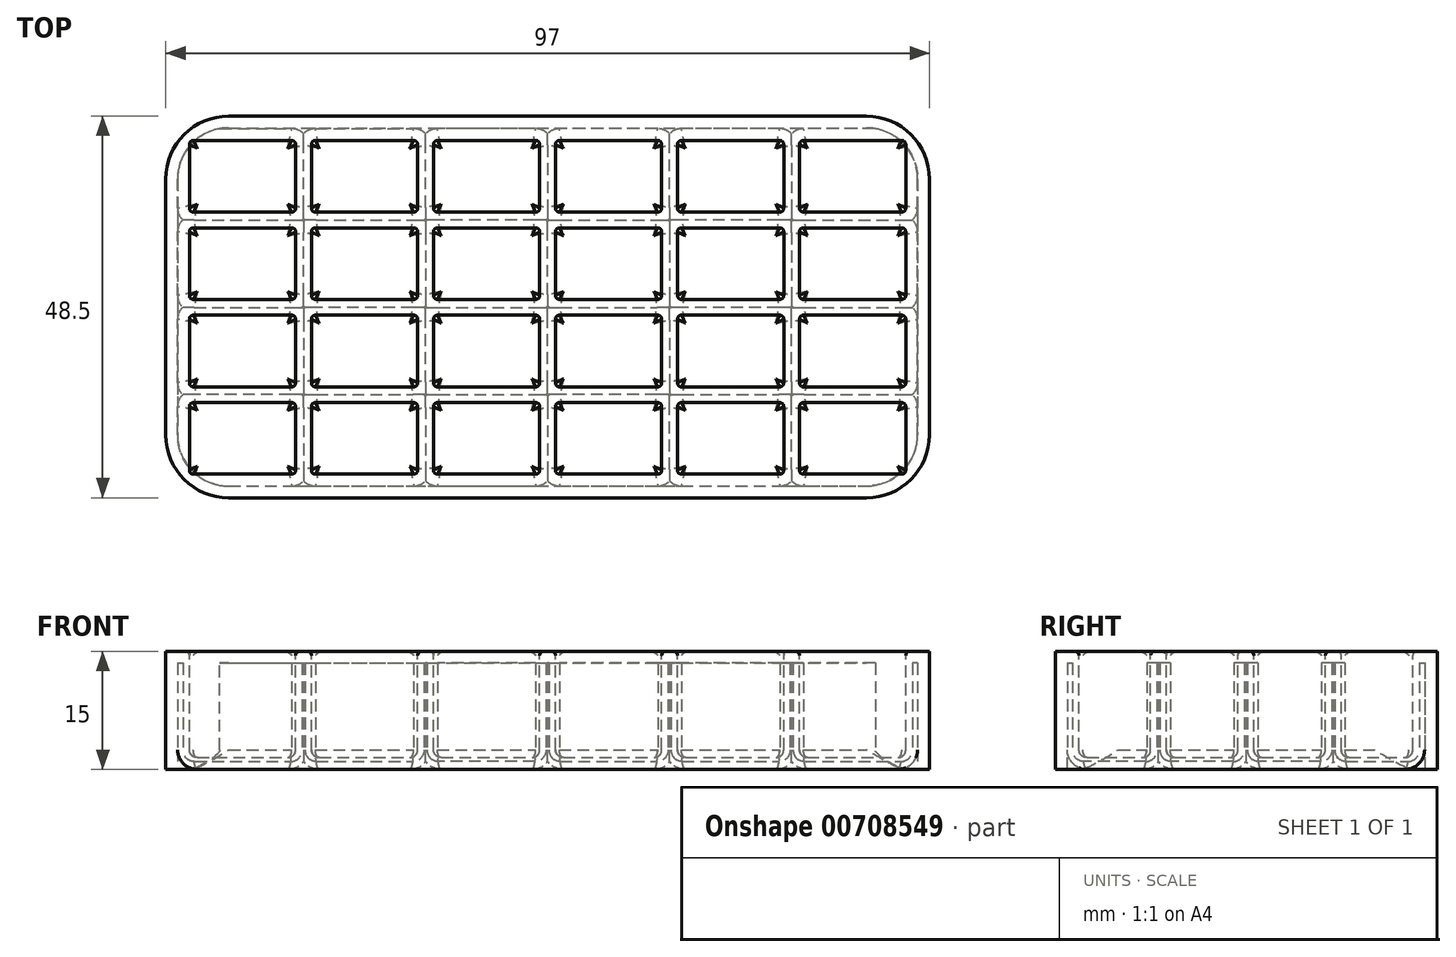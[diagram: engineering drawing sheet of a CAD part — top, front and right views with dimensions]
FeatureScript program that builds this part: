
annotation { "Feature Type Name" : "Feature", "Feature Type Description" : "" }
export const myFeature = defineFeature(function(context is Context, id is Id, definition is map)
    precondition{}
    {
        {
            var Q0;
            Q0=qCreatedBy(makeId("Top.planeOp"),FACE);
            var sketch = newSketch(context, id + "F0", { "sketchPlane" : qUnion([Q0])});
            skLineSegment(sketch, "E0.bottom", {"start": v(-13.12, 43.46) * mm, "end": v(83.88, 43.46) * mm});
            skLineSegment(sketch, "E0.top", {"start": v(-13.12, -5.04) * mm, "end": v(83.88, -5.04) * mm});
            skLineSegment(sketch, "E0.left", {"start": v(-13.12, 43.46) * mm, "end": v(-13.12, -5.04) * mm});
            skLineSegment(sketch, "E0.right", {"start": v(83.88, 43.46) * mm, "end": v(83.88, -5.04) * mm});
            skSolve(sketch);
        }
        {
            var Q0;
            Q0=makeQuery(id+"F0.imprint","IMPRINT",FACE,{"disambiguationData":[TD([[makeQuery(id+"F0.imprint","IMPRINT",EDGE,{"derivedFrom":sQuery(id+"F0.wireOp",EDGE,"E0.bottom")}),-1.0]])]});
            extrude(context, id + "F1", {"entities" : qUnion([Q0]), "depth" : 15 * mm, "offsetDistance" : 25.4 * mm});
        }
        {
            var Q0;
            Q0=makeQuery(id+"F1.opExtrude","CAP_FACE",FACE,{"disambiguationData":[OSD([sQuery(id+"F0.wireOp",EDGE,"E0.bottom"),sQuery(id+"F0.wireOp",EDGE,"E0.top"),sQuery(id+"F0.wireOp",EDGE,"E0.left"),sQuery(id+"F0.wireOp",EDGE,"E0.right")])],"isStart":false});
            var sketch = newSketch(context, id + "F2", { "sketchPlane" : qUnion([Q0])});
            skLineSegment(sketch, "E1.bottom", {"start": v(-10.12, -2.04) * mm, "end": v(3.38, -2.04) * mm});
            skLineSegment(sketch, "E1.top", {"start": v(-10.12, 7.06) * mm, "end": v(3.38, 7.06) * mm});
            skLineSegment(sketch, "E1.left", {"start": v(-10.12, -2.04) * mm, "end": v(-10.12, 7.06) * mm});
            skLineSegment(sketch, "E1.right", {"start": v(3.38, -2.04) * mm, "end": v(3.38, 7.06) * mm});
            skLineSegment(sketch, "E2.1.0.0", {"start": v(18.88, -2.04) * mm, "end": v(18.88, 7.06) * mm});
            skLineSegment(sketch, "E2.1.0.1", {"start": v(5.38, 7.06) * mm, "end": v(18.88, 7.06) * mm});
            skLineSegment(sketch, "E2.1.0.2", {"start": v(5.38, -2.04) * mm, "end": v(5.38, 7.06) * mm});
            skLineSegment(sketch, "E2.1.0.3", {"start": v(5.38, -2.04) * mm, "end": v(18.88, -2.04) * mm});
            skLineSegment(sketch, "E2.2.0.0", {"start": v(34.38, -2.04) * mm, "end": v(34.38, 7.06) * mm});
            skLineSegment(sketch, "E2.2.0.1", {"start": v(20.88, 7.06) * mm, "end": v(34.38, 7.06) * mm});
            skLineSegment(sketch, "E2.2.0.2", {"start": v(20.88, -2.04) * mm, "end": v(20.88, 7.06) * mm});
            skLineSegment(sketch, "E2.2.0.3", {"start": v(20.88, -2.04) * mm, "end": v(34.38, -2.04) * mm});
            skLineSegment(sketch, "E2.3.0.0", {"start": v(49.88, -2.04) * mm, "end": v(49.88, 7.06) * mm});
            skLineSegment(sketch, "E2.3.0.1", {"start": v(36.38, 7.06) * mm, "end": v(49.88, 7.06) * mm});
            skLineSegment(sketch, "E2.3.0.2", {"start": v(36.38, -2.04) * mm, "end": v(36.38, 7.06) * mm});
            skLineSegment(sketch, "E2.3.0.3", {"start": v(36.38, -2.04) * mm, "end": v(49.88, -2.04) * mm});
            skLineSegment(sketch, "E2.4.0.0", {"start": v(65.38, -2.04) * mm, "end": v(65.38, 7.06) * mm});
            skLineSegment(sketch, "E2.4.0.1", {"start": v(51.88, 7.06) * mm, "end": v(65.38, 7.06) * mm});
            skLineSegment(sketch, "E2.4.0.2", {"start": v(51.88, -2.04) * mm, "end": v(51.88, 7.06) * mm});
            skLineSegment(sketch, "E2.4.0.3", {"start": v(51.88, -2.04) * mm, "end": v(65.38, -2.04) * mm});
            skLineSegment(sketch, "E2.5.0.0", {"start": v(80.88, -2.04) * mm, "end": v(80.88, 7.06) * mm});
            skLineSegment(sketch, "E2.5.0.1", {"start": v(67.38, 7.06) * mm, "end": v(80.88, 7.06) * mm});
            skLineSegment(sketch, "E2.5.0.2", {"start": v(67.38, -2.04) * mm, "end": v(67.38, 7.06) * mm});
            skLineSegment(sketch, "E2.5.0.3", {"start": v(67.38, -2.04) * mm, "end": v(80.88, -2.04) * mm});
            skLineSegment(sketch, "E2.direction1", {"start": v(3.38, -2.04) * mm, "end": v(18.88, -2.04) * mm, "construction": true});
            skLineSegment(sketch, "E3.1.0.0", {"start": v(20.88, 9.06) * mm, "end": v(34.38, 9.06) * mm});
            skLineSegment(sketch, "E3.1.0.1", {"start": v(20.88, 9.06) * mm, "end": v(20.88, 18.16) * mm});
            skLineSegment(sketch, "E3.1.0.2", {"start": v(20.88, 18.16) * mm, "end": v(34.38, 18.16) * mm});
            skLineSegment(sketch, "E3.1.0.3", {"start": v(34.38, 9.06) * mm, "end": v(34.38, 18.16) * mm});
            skLineSegment(sketch, "E3.1.0.4", {"start": v(3.38, 9.06) * mm, "end": v(3.38, 18.16) * mm});
            skLineSegment(sketch, "E3.1.0.5", {"start": v(-10.12, 9.06) * mm, "end": v(-10.12, 18.16) * mm});
            skLineSegment(sketch, "E3.1.0.6", {"start": v(-10.12, 18.16) * mm, "end": v(3.38, 18.16) * mm});
            skLineSegment(sketch, "E3.1.0.7", {"start": v(36.38, 9.06) * mm, "end": v(36.38, 18.16) * mm});
            skLineSegment(sketch, "E3.1.0.8", {"start": v(-10.12, 9.06) * mm, "end": v(3.38, 9.06) * mm});
            skLineSegment(sketch, "E3.1.0.9", {"start": v(36.38, 18.16) * mm, "end": v(49.88, 18.16) * mm});
            skLineSegment(sketch, "E3.1.0.10", {"start": v(51.88, 9.06) * mm, "end": v(51.88, 18.16) * mm});
            skLineSegment(sketch, "E3.1.0.11", {"start": v(65.38, 9.06) * mm, "end": v(65.38, 18.16) * mm});
            skLineSegment(sketch, "E3.1.0.12", {"start": v(67.38, 18.16) * mm, "end": v(80.88, 18.16) * mm});
            skLineSegment(sketch, "E3.1.0.13", {"start": v(51.88, 9.06) * mm, "end": v(65.38, 9.06) * mm});
            skLineSegment(sketch, "E3.1.0.14", {"start": v(67.38, 9.06) * mm, "end": v(67.38, 18.16) * mm});
            skLineSegment(sketch, "E3.1.0.15", {"start": v(18.88, 9.06) * mm, "end": v(18.88, 18.16) * mm});
            skLineSegment(sketch, "E3.1.0.16", {"start": v(5.38, 18.16) * mm, "end": v(18.88, 18.16) * mm});
            skLineSegment(sketch, "E3.1.0.17", {"start": v(67.38, 9.06) * mm, "end": v(80.88, 9.06) * mm});
            skLineSegment(sketch, "E3.1.0.18", {"start": v(36.38, 9.06) * mm, "end": v(49.88, 9.06) * mm});
            skLineSegment(sketch, "E3.1.0.19", {"start": v(49.88, 9.06) * mm, "end": v(49.88, 18.16) * mm});
            skLineSegment(sketch, "E3.1.0.20", {"start": v(80.88, 9.06) * mm, "end": v(80.88, 18.16) * mm});
            skLineSegment(sketch, "E3.1.0.21", {"start": v(5.38, 9.06) * mm, "end": v(5.38, 18.16) * mm});
            skLineSegment(sketch, "E3.1.0.22", {"start": v(51.88, 18.16) * mm, "end": v(65.38, 18.16) * mm});
            skLineSegment(sketch, "E3.1.0.23", {"start": v(3.38, 9.06) * mm, "end": v(18.88, 9.06) * mm, "construction": true});
            skLineSegment(sketch, "E3.1.0.24", {"start": v(5.38, 9.06) * mm, "end": v(18.88, 9.06) * mm});
            skLineSegment(sketch, "E3.2.0.0", {"start": v(20.88, 20.16) * mm, "end": v(34.38, 20.16) * mm});
            skLineSegment(sketch, "E3.2.0.1", {"start": v(20.88, 20.16) * mm, "end": v(20.88, 29.26) * mm});
            skLineSegment(sketch, "E3.2.0.2", {"start": v(20.88, 29.26) * mm, "end": v(34.38, 29.26) * mm});
            skLineSegment(sketch, "E3.2.0.3", {"start": v(34.38, 20.16) * mm, "end": v(34.38, 29.26) * mm});
            skLineSegment(sketch, "E3.2.0.4", {"start": v(3.38, 20.16) * mm, "end": v(3.38, 29.26) * mm});
            skLineSegment(sketch, "E3.2.0.5", {"start": v(-10.12, 20.16) * mm, "end": v(-10.12, 29.26) * mm});
            skLineSegment(sketch, "E3.2.0.6", {"start": v(-10.12, 29.26) * mm, "end": v(3.38, 29.26) * mm});
            skLineSegment(sketch, "E3.2.0.7", {"start": v(36.38, 20.16) * mm, "end": v(36.38, 29.26) * mm});
            skLineSegment(sketch, "E3.2.0.8", {"start": v(-10.12, 20.16) * mm, "end": v(3.38, 20.16) * mm});
            skLineSegment(sketch, "E3.2.0.9", {"start": v(36.38, 29.26) * mm, "end": v(49.88, 29.26) * mm});
            skLineSegment(sketch, "E3.2.0.10", {"start": v(51.88, 20.16) * mm, "end": v(51.88, 29.26) * mm});
            skLineSegment(sketch, "E3.2.0.11", {"start": v(65.38, 20.16) * mm, "end": v(65.38, 29.26) * mm});
            skLineSegment(sketch, "E3.2.0.12", {"start": v(67.38, 29.26) * mm, "end": v(80.88, 29.26) * mm});
            skLineSegment(sketch, "E3.2.0.13", {"start": v(51.88, 20.16) * mm, "end": v(65.38, 20.16) * mm});
            skLineSegment(sketch, "E3.2.0.14", {"start": v(67.38, 20.16) * mm, "end": v(67.38, 29.26) * mm});
            skLineSegment(sketch, "E3.2.0.15", {"start": v(18.88, 20.16) * mm, "end": v(18.88, 29.26) * mm});
            skLineSegment(sketch, "E3.2.0.16", {"start": v(5.38, 29.26) * mm, "end": v(18.88, 29.26) * mm});
            skLineSegment(sketch, "E3.2.0.17", {"start": v(67.38, 20.16) * mm, "end": v(80.88, 20.16) * mm});
            skLineSegment(sketch, "E3.2.0.18", {"start": v(36.38, 20.16) * mm, "end": v(49.88, 20.16) * mm});
            skLineSegment(sketch, "E3.2.0.19", {"start": v(49.88, 20.16) * mm, "end": v(49.88, 29.26) * mm});
            skLineSegment(sketch, "E3.2.0.20", {"start": v(80.88, 20.16) * mm, "end": v(80.88, 29.26) * mm});
            skLineSegment(sketch, "E3.2.0.21", {"start": v(5.38, 20.16) * mm, "end": v(5.38, 29.26) * mm});
            skLineSegment(sketch, "E3.2.0.22", {"start": v(51.88, 29.26) * mm, "end": v(65.38, 29.26) * mm});
            skLineSegment(sketch, "E3.2.0.23", {"start": v(3.38, 20.16) * mm, "end": v(18.88, 20.16) * mm, "construction": true});
            skLineSegment(sketch, "E3.2.0.24", {"start": v(5.38, 20.16) * mm, "end": v(18.88, 20.16) * mm});
            skLineSegment(sketch, "E3.direction1", {"start": v(-10.12, -2.04) * mm, "end": v(-10.12, 9.06) * mm, "construction": true});
            skLineSegment(sketch, "E4.0.3.0", {"start": v(20.88, 31.26) * mm, "end": v(34.38, 31.26) * mm});
            skLineSegment(sketch, "E4.3.3.0", {"start": v(20.88, 31.26) * mm, "end": v(20.88, 40.36) * mm});
            skLineSegment(sketch, "E4.6.3.0", {"start": v(20.88, 40.36) * mm, "end": v(34.38, 40.36) * mm});
            skLineSegment(sketch, "E4.9.3.0", {"start": v(34.38, 31.26) * mm, "end": v(34.38, 40.36) * mm});
            skLineSegment(sketch, "E4.12.3.0", {"start": v(3.38, 31.26) * mm, "end": v(3.38, 40.36) * mm});
            skLineSegment(sketch, "E4.15.3.0", {"start": v(-10.12, 31.26) * mm, "end": v(-10.12, 40.36) * mm});
            skLineSegment(sketch, "E4.18.3.0", {"start": v(-10.12, 40.36) * mm, "end": v(3.38, 40.36) * mm});
            skLineSegment(sketch, "E4.21.3.0", {"start": v(36.38, 31.26) * mm, "end": v(36.38, 40.36) * mm});
            skLineSegment(sketch, "E4.24.3.0", {"start": v(-10.12, 31.26) * mm, "end": v(3.38, 31.26) * mm});
            skLineSegment(sketch, "E4.27.3.0", {"start": v(36.38, 40.36) * mm, "end": v(49.88, 40.36) * mm});
            skLineSegment(sketch, "E4.30.3.0", {"start": v(51.88, 31.26) * mm, "end": v(51.88, 40.36) * mm});
            skLineSegment(sketch, "E4.33.3.0", {"start": v(65.38, 31.26) * mm, "end": v(65.38, 40.36) * mm});
            skLineSegment(sketch, "E4.36.3.0", {"start": v(67.38, 40.36) * mm, "end": v(80.88, 40.36) * mm});
            skLineSegment(sketch, "E4.39.3.0", {"start": v(51.88, 31.26) * mm, "end": v(65.38, 31.26) * mm});
            skLineSegment(sketch, "E4.42.3.0", {"start": v(67.38, 31.26) * mm, "end": v(67.38, 40.36) * mm});
            skLineSegment(sketch, "E4.45.3.0", {"start": v(18.88, 31.26) * mm, "end": v(18.88, 40.36) * mm});
            skLineSegment(sketch, "E4.48.3.0", {"start": v(5.38, 40.36) * mm, "end": v(18.88, 40.36) * mm});
            skLineSegment(sketch, "E4.51.3.0", {"start": v(67.38, 31.26) * mm, "end": v(80.88, 31.26) * mm});
            skLineSegment(sketch, "E4.54.3.0", {"start": v(36.38, 31.26) * mm, "end": v(49.88, 31.26) * mm});
            skLineSegment(sketch, "E4.57.3.0", {"start": v(49.88, 31.26) * mm, "end": v(49.88, 40.36) * mm});
            skLineSegment(sketch, "E4.60.3.0", {"start": v(80.88, 31.26) * mm, "end": v(80.88, 40.36) * mm});
            skLineSegment(sketch, "E4.63.3.0", {"start": v(5.38, 31.26) * mm, "end": v(5.38, 40.36) * mm});
            skLineSegment(sketch, "E4.66.3.0", {"start": v(51.88, 40.36) * mm, "end": v(65.38, 40.36) * mm});
            skLineSegment(sketch, "E4.69.3.0", {"start": v(3.38, 31.26) * mm, "end": v(18.88, 31.26) * mm, "construction": true});
            skLineSegment(sketch, "E4.72.3.0", {"start": v(5.38, 31.26) * mm, "end": v(18.88, 31.26) * mm});
            skSolve(sketch);
        }
        {
            var Q0;
            Q0=makeQuery(id+"F2.imprint","IMPRINT",FACE,{"disambiguationData":[TD([[makeQuery(id+"F2.imprint","IMPRINT",EDGE,{"derivedFrom":sQuery(id+"F2.wireOp",EDGE,"E1.bottom")}),1.0]])]});
            var Q1;
            Q1=makeQuery(id+"F2.imprint","IMPRINT",FACE,{"disambiguationData":[TD([[makeQuery(id+"F2.imprint","IMPRINT",EDGE,{"derivedFrom":sQuery(id+"F2.wireOp",EDGE,"E2.1.0.0")}),1.0]])]});
            var Q2;
            Q2=makeQuery(id+"F2.imprint","IMPRINT",FACE,{"disambiguationData":[TD([[makeQuery(id+"F2.imprint","IMPRINT",EDGE,{"derivedFrom":sQuery(id+"F2.wireOp",EDGE,"E2.2.0.0")}),1.0]])]});
            var Q3;
            Q3=makeQuery(id+"F2.imprint","IMPRINT",FACE,{"disambiguationData":[TD([[makeQuery(id+"F2.imprint","IMPRINT",EDGE,{"derivedFrom":sQuery(id+"F2.wireOp",EDGE,"E2.3.0.0")}),1.0]])]});
            var Q4;
            Q4=makeQuery(id+"F2.imprint","IMPRINT",FACE,{"disambiguationData":[TD([[makeQuery(id+"F2.imprint","IMPRINT",EDGE,{"derivedFrom":sQuery(id+"F2.wireOp",EDGE,"E2.4.0.0")}),1.0]])]});
            var Q5;
            Q5=makeQuery(id+"F2.imprint","IMPRINT",FACE,{"disambiguationData":[TD([[makeQuery(id+"F2.imprint","IMPRINT",EDGE,{"derivedFrom":sQuery(id+"F2.wireOp",EDGE,"E2.5.0.0")}),1.0]])]});
            var Q6;
            Q6=makeQuery(id+"F2.imprint","IMPRINT",FACE,{"disambiguationData":[TD([[makeQuery(id+"F2.imprint","IMPRINT",EDGE,{"derivedFrom":sQuery(id+"F2.wireOp",EDGE,"E3.1.0.4")}),1.0]])]});
            var Q7;
            Q7=makeQuery(id+"F2.imprint","IMPRINT",FACE,{"disambiguationData":[TD([[makeQuery(id+"F2.imprint","IMPRINT",EDGE,{"derivedFrom":sQuery(id+"F2.wireOp",EDGE,"E3.1.0.15")}),1.0]])]});
            var Q8;
            Q8=makeQuery(id+"F2.imprint","IMPRINT",FACE,{"disambiguationData":[TD([[makeQuery(id+"F2.imprint","IMPRINT",EDGE,{"derivedFrom":sQuery(id+"F2.wireOp",EDGE,"E3.2.0.7")}),-1.0]])]});
            var Q9;
            Q9=makeQuery(id+"F2.imprint","IMPRINT",FACE,{"disambiguationData":[TD([[makeQuery(id+"F2.imprint","IMPRINT",EDGE,{"derivedFrom":sQuery(id+"F2.wireOp",EDGE,"E3.1.0.0")}),1.0]])]});
            var Q10;
            Q10=makeQuery(id+"F2.imprint","IMPRINT",FACE,{"disambiguationData":[TD([[makeQuery(id+"F2.imprint","IMPRINT",EDGE,{"derivedFrom":sQuery(id+"F2.wireOp",EDGE,"E3.1.0.7")}),-1.0]])]});
            var Q11;
            Q11=makeQuery(id+"F2.imprint","IMPRINT",FACE,{"disambiguationData":[TD([[makeQuery(id+"F2.imprint","IMPRINT",EDGE,{"derivedFrom":sQuery(id+"F2.wireOp",EDGE,"E3.1.0.10")}),-1.0]])]});
            var Q12;
            Q12=makeQuery(id+"F2.imprint","IMPRINT",FACE,{"disambiguationData":[TD([[makeQuery(id+"F2.imprint","IMPRINT",EDGE,{"derivedFrom":sQuery(id+"F2.wireOp",EDGE,"E3.1.0.12")}),-1.0]])]});
            var Q13;
            Q13=makeQuery(id+"F2.imprint","IMPRINT",FACE,{"disambiguationData":[TD([[makeQuery(id+"F2.imprint","IMPRINT",EDGE,{"derivedFrom":sQuery(id+"F2.wireOp",EDGE,"E3.2.0.12")}),-1.0]])]});
            var Q14;
            Q14=makeQuery(id+"F2.imprint","IMPRINT",FACE,{"disambiguationData":[TD([[makeQuery(id+"F2.imprint","IMPRINT",EDGE,{"derivedFrom":sQuery(id+"F2.wireOp",EDGE,"E3.2.0.10")}),-1.0]])]});
            var Q15;
            Q15=makeQuery(id+"F2.imprint","IMPRINT",FACE,{"disambiguationData":[TD([[makeQuery(id+"F2.imprint","IMPRINT",EDGE,{"derivedFrom":sQuery(id+"F2.wireOp",EDGE,"E3.2.0.0")}),1.0]])]});
            var Q16;
            Q16=makeQuery(id+"F2.imprint","IMPRINT",FACE,{"disambiguationData":[TD([[makeQuery(id+"F2.imprint","IMPRINT",EDGE,{"derivedFrom":sQuery(id+"F2.wireOp",EDGE,"E3.2.0.15")}),1.0]])]});
            var Q17;
            Q17=makeQuery(id+"F2.imprint","IMPRINT",FACE,{"disambiguationData":[TD([[makeQuery(id+"F2.imprint","IMPRINT",EDGE,{"derivedFrom":sQuery(id+"F2.wireOp",EDGE,"E3.2.0.4")}),1.0]])]});
            var Q18;
            Q18=makeQuery(id+"F2.imprint","IMPRINT",FACE,{"disambiguationData":[TD([[makeQuery(id+"F2.imprint","IMPRINT",EDGE,{"derivedFrom":sQuery(id+"F2.wireOp",EDGE,"2d819ab5-a139-4a24-9444-a94bec9d9159.0.2.2")}),1.0]])]});
            var Q19;
            Q19=makeQuery(id+"F2.imprint","IMPRINT",FACE,{"disambiguationData":[TD([[makeQuery(id+"F2.imprint","IMPRINT",EDGE,{"derivedFrom":sQuery(id+"F2.wireOp",EDGE,"2d819ab5-a139-4a24-9444-a94bec9d9159.0.2.0")}),1.0]])]});
            var Q20;
            Q20=makeQuery(id+"F2.imprint","IMPRINT",FACE,{"disambiguationData":[TD([[makeQuery(id+"F2.imprint","IMPRINT",EDGE,{"derivedFrom":sQuery(id+"F2.wireOp",EDGE,"2d819ab5-a139-4a24-9444-a94bec9d9159.0.1.0")}),1.0]])]});
            var Q21;
            Q21=makeQuery(id+"F2.imprint","IMPRINT",FACE,{"disambiguationData":[TD([[makeQuery(id+"F2.imprint","IMPRINT",EDGE,{"derivedFrom":sQuery(id+"F2.wireOp",EDGE,"c4168fa5-6cb4-4a63-8e2b-b4d674aba8b3.0.7.0")}),1.0]])]});
            var Q22;
            Q22=makeQuery(id+"F2.imprint","IMPRINT",FACE,{"disambiguationData":[TD([[makeQuery(id+"F2.imprint","IMPRINT",EDGE,{"derivedFrom":sQuery(id+"F2.wireOp",EDGE,"c4168fa5-6cb4-4a63-8e2b-b4d674aba8b3.0.6.0")}),1.0]])]});
            var Q23;
            Q23=makeQuery(id+"F2.imprint","IMPRINT",FACE,{"disambiguationData":[TD([[makeQuery(id+"F2.imprint","IMPRINT",EDGE,{"derivedFrom":sQuery(id+"F2.wireOp",EDGE,"2d819ab5-a139-4a24-9444-a94bec9d9159.0.1.2")}),1.0]])]});
            var Q24;
            Q24=makeQuery(id+"F2.imprint","IMPRINT",FACE,{"disambiguationData":[TD([[makeQuery(id+"F2.imprint","IMPRINT",EDGE,{"derivedFrom":sQuery(id+"F2.wireOp",EDGE,"E4.36.3.0")}),-1.0]])]});
            var Q25;
            Q25=makeQuery(id+"F2.imprint","IMPRINT",FACE,{"disambiguationData":[TD([[makeQuery(id+"F2.imprint","IMPRINT",EDGE,{"derivedFrom":sQuery(id+"F2.wireOp",EDGE,"E4.30.3.0")}),-1.0]])]});
            var Q26;
            Q26=makeQuery(id+"F2.imprint","IMPRINT",FACE,{"disambiguationData":[TD([[makeQuery(id+"F2.imprint","IMPRINT",EDGE,{"derivedFrom":sQuery(id+"F2.wireOp",EDGE,"E4.21.3.0")}),-1.0]])]});
            var Q27;
            Q27=makeQuery(id+"F2.imprint","IMPRINT",FACE,{"disambiguationData":[TD([[makeQuery(id+"F2.imprint","IMPRINT",EDGE,{"derivedFrom":sQuery(id+"F2.wireOp",EDGE,"E4.0.3.0")}),1.0]])]});
            var Q28;
            Q28=makeQuery(id+"F2.imprint","IMPRINT",FACE,{"disambiguationData":[TD([[makeQuery(id+"F2.imprint","IMPRINT",EDGE,{"derivedFrom":sQuery(id+"F2.wireOp",EDGE,"E4.45.3.0")}),1.0]])]});
            var Q29;
            Q29=makeQuery(id+"F2.imprint","IMPRINT",FACE,{"disambiguationData":[TD([[makeQuery(id+"F2.imprint","IMPRINT",EDGE,{"derivedFrom":sQuery(id+"F2.wireOp",EDGE,"E4.12.3.0")}),1.0]])]});
            extrude(context, id + "F3", {"entities" : qUnion([Q0, Q1, Q2, Q3, Q4, Q5, Q6, Q7, Q8, Q9, Q10, Q11, Q12, Q13, Q14, Q15, Q16, Q17, Q18, Q19, Q20, Q21, Q22, Q23, Q24, Q25, Q26, Q27, Q28, Q29]), "operationType" : NewBodyOperationType.REMOVE, "oppositeDirection" : true, "depth" : 13.5 * mm, "offsetDistance" : 25 * mm});
        }
        {
            var Q0;
            Q0=makeQuery(id+"F1.opExtrude","SWEPT_EDGE",EDGE,{"disambiguationData":[OSD([sQuery(id+"F0.wireOp",EDGE,"E0.top"),sQuery(id+"F0.wireOp",EDGE,"E0.left")])]});
            var Q1;
            Q1=makeQuery(id+"F1.opExtrude","SWEPT_EDGE",EDGE,{"disambiguationData":[OSD([sQuery(id+"F0.wireOp",EDGE,"E0.top"),sQuery(id+"F0.wireOp",EDGE,"E0.right")])]});
            var Q2;
            Q2=makeQuery(id+"F1.opExtrude","SWEPT_EDGE",EDGE,{"disambiguationData":[OSD([sQuery(id+"F0.wireOp",EDGE,"E0.bottom"),sQuery(id+"F0.wireOp",EDGE,"E0.right")])]});
            var Q3;
            Q3=makeQuery(id+"F1.opExtrude","SWEPT_EDGE",EDGE,{"disambiguationData":[OSD([sQuery(id+"F0.wireOp",EDGE,"E0.bottom"),sQuery(id+"F0.wireOp",EDGE,"E0.left")])]});
            fillet(context, id + "F4", {"entities" : qUnion([Q0, Q1, Q2, Q3]), "radius" : 8 * mm, "tangentPropagation" : true, "allowEdgeOverflow" : false});
        }
        {
            var Q0;
            Q0=makeQuery(id+"F3.boolean.opBoolean","COPY",EDGE,{"derivedFrom":makeQuery(id+"F3.opExtrude","CAP_EDGE",EDGE,{"disambiguationData":[OSD([sQuery(id+"F2.wireOp",EDGE,"E3.1.0.22")])],"isStart":false})});
            var Q1;
            Q1=makeQuery(id+"F3.boolean.opBoolean","COPY",EDGE,{"derivedFrom":makeQuery(id+"F3.opExtrude","CAP_EDGE",EDGE,{"disambiguationData":[OSD([sQuery(id+"F2.wireOp",EDGE,"E3.1.0.11")])],"isStart":false})});
            var Q2;
            Q2=makeQuery(id+"F3.boolean.opBoolean","COPY",EDGE,{"derivedFrom":makeQuery(id+"F3.opExtrude","CAP_EDGE",EDGE,{"disambiguationData":[OSD([sQuery(id+"F2.wireOp",EDGE,"E3.1.0.13")])],"isStart":false})});
            var Q3;
            Q3=makeQuery(id+"F3.boolean.opBoolean","COPY",EDGE,{"derivedFrom":makeQuery(id+"F3.opExtrude","CAP_EDGE",EDGE,{"disambiguationData":[OSD([sQuery(id+"F2.wireOp",EDGE,"E3.1.0.10")])],"isStart":false})});
            var Q4;
            Q4=makeQuery(id+"F3.boolean.opBoolean","COPY",EDGE,{"derivedFrom":makeQuery(id+"F3.opExtrude","CAP_EDGE",EDGE,{"disambiguationData":[OSD([sQuery(id+"F2.wireOp",EDGE,"E3.2.0.22")])],"isStart":false})});
            var Q5;
            Q5=makeQuery(id+"F3.boolean.opBoolean","COPY",EDGE,{"derivedFrom":makeQuery(id+"F3.opExtrude","CAP_EDGE",EDGE,{"disambiguationData":[OSD([sQuery(id+"F2.wireOp",EDGE,"E3.2.0.11")])],"isStart":false})});
            var Q6;
            Q6=makeQuery(id+"F3.boolean.opBoolean","COPY",FACE,{"derivedFrom":makeQuery(id+"F3.opExtrude","CAP_FACE",FACE,{"disambiguationData":[OSD([sQuery(id+"F2.wireOp",EDGE,"E3.2.0.10"),sQuery(id+"F2.wireOp",EDGE,"E3.2.0.11"),sQuery(id+"F2.wireOp",EDGE,"E3.2.0.13"),sQuery(id+"F2.wireOp",EDGE,"E3.2.0.22")])],"isStart":false})});
            var Q7;
            Q7=makeQuery(id+"F3.boolean.opBoolean","COPY",FACE,{"derivedFrom":makeQuery(id+"F3.opExtrude","CAP_FACE",FACE,{"disambiguationData":[OSD([sQuery(id+"F2.wireOp",EDGE,"E2.4.0.0"),sQuery(id+"F2.wireOp",EDGE,"E2.4.0.1"),sQuery(id+"F2.wireOp",EDGE,"E2.4.0.2"),sQuery(id+"F2.wireOp",EDGE,"E2.4.0.3")])],"isStart":false})});
            var Q8;
            Q8=makeQuery(id+"F3.boolean.opBoolean","COPY",FACE,{"derivedFrom":makeQuery(id+"F3.opExtrude","CAP_FACE",FACE,{"disambiguationData":[OSD([sQuery(id+"F2.wireOp",EDGE,"E2.3.0.0"),sQuery(id+"F2.wireOp",EDGE,"E2.3.0.1"),sQuery(id+"F2.wireOp",EDGE,"E2.3.0.2"),sQuery(id+"F2.wireOp",EDGE,"E2.3.0.3")])],"isStart":false})});
            var Q9;
            Q9=makeQuery(id+"F3.boolean.opBoolean","COPY",FACE,{"derivedFrom":makeQuery(id+"F3.opExtrude","CAP_FACE",FACE,{"disambiguationData":[OSD([sQuery(id+"F2.wireOp",EDGE,"E3.1.0.7"),sQuery(id+"F2.wireOp",EDGE,"E3.1.0.9"),sQuery(id+"F2.wireOp",EDGE,"E3.1.0.18"),sQuery(id+"F2.wireOp",EDGE,"E3.1.0.19")])],"isStart":false})});
            var Q10;
            Q10=makeQuery(id+"F3.boolean.opBoolean","COPY",FACE,{"derivedFrom":makeQuery(id+"F3.opExtrude","CAP_FACE",FACE,{"disambiguationData":[OSD([sQuery(id+"F2.wireOp",EDGE,"E3.2.0.7"),sQuery(id+"F2.wireOp",EDGE,"E3.2.0.9"),sQuery(id+"F2.wireOp",EDGE,"E3.2.0.18"),sQuery(id+"F2.wireOp",EDGE,"E3.2.0.19")])],"isStart":false})});
            var Q11;
            Q11=makeQuery(id+"F3.boolean.opBoolean","COPY",FACE,{"derivedFrom":makeQuery(id+"F3.opExtrude","CAP_FACE",FACE,{"disambiguationData":[OSD([sQuery(id+"F2.wireOp",EDGE,"E3.2.0.0"),sQuery(id+"F2.wireOp",EDGE,"E3.2.0.1"),sQuery(id+"F2.wireOp",EDGE,"E3.2.0.2"),sQuery(id+"F2.wireOp",EDGE,"E3.2.0.3")])],"isStart":false})});
            var Q12;
            Q12=makeQuery(id+"F3.boolean.opBoolean","COPY",FACE,{"derivedFrom":makeQuery(id+"F3.opExtrude","CAP_FACE",FACE,{"disambiguationData":[OSD([sQuery(id+"F2.wireOp",EDGE,"E3.1.0.0"),sQuery(id+"F2.wireOp",EDGE,"E3.1.0.1"),sQuery(id+"F2.wireOp",EDGE,"E3.1.0.2"),sQuery(id+"F2.wireOp",EDGE,"E3.1.0.3")])],"isStart":false})});
            var Q13;
            Q13=makeQuery(id+"F3.boolean.opBoolean","COPY",FACE,{"derivedFrom":makeQuery(id+"F3.opExtrude","CAP_FACE",FACE,{"disambiguationData":[OSD([sQuery(id+"F2.wireOp",EDGE,"E2.2.0.0"),sQuery(id+"F2.wireOp",EDGE,"E2.2.0.1"),sQuery(id+"F2.wireOp",EDGE,"E2.2.0.2"),sQuery(id+"F2.wireOp",EDGE,"E2.2.0.3")])],"isStart":false})});
            var Q14;
            Q14=makeQuery(id+"F3.boolean.opBoolean","COPY",FACE,{"derivedFrom":makeQuery(id+"F3.opExtrude","CAP_FACE",FACE,{"disambiguationData":[OSD([sQuery(id+"F2.wireOp",EDGE,"E2.1.0.0"),sQuery(id+"F2.wireOp",EDGE,"E2.1.0.1"),sQuery(id+"F2.wireOp",EDGE,"E2.1.0.2"),sQuery(id+"F2.wireOp",EDGE,"E2.1.0.3")])],"isStart":false})});
            var Q15;
            Q15=makeQuery(id+"F3.boolean.opBoolean","COPY",FACE,{"derivedFrom":makeQuery(id+"F3.opExtrude","CAP_FACE",FACE,{"disambiguationData":[OSD([sQuery(id+"F2.wireOp",EDGE,"E3.1.0.4"),sQuery(id+"F2.wireOp",EDGE,"E3.1.0.5"),sQuery(id+"F2.wireOp",EDGE,"E3.1.0.6"),sQuery(id+"F2.wireOp",EDGE,"E3.1.0.8")])],"isStart":false})});
            var Q16;
            Q16=makeQuery(id+"F3.boolean.opBoolean","COPY",FACE,{"derivedFrom":makeQuery(id+"F3.opExtrude","CAP_FACE",FACE,{"disambiguationData":[OSD([sQuery(id+"F2.wireOp",EDGE,"E3.1.0.15"),sQuery(id+"F2.wireOp",EDGE,"E3.1.0.16"),sQuery(id+"F2.wireOp",EDGE,"E3.1.0.21"),sQuery(id+"F2.wireOp",EDGE,"E3.1.0.24")])],"isStart":false})});
            var Q17;
            Q17=makeQuery(id+"F3.boolean.opBoolean","COPY",FACE,{"derivedFrom":makeQuery(id+"F3.opExtrude","CAP_FACE",FACE,{"disambiguationData":[OSD([sQuery(id+"F2.wireOp",EDGE,"E3.2.0.15"),sQuery(id+"F2.wireOp",EDGE,"E3.2.0.16"),sQuery(id+"F2.wireOp",EDGE,"E3.2.0.21"),sQuery(id+"F2.wireOp",EDGE,"E3.2.0.24")])],"isStart":false})});
            var Q18;
            Q18=makeQuery(id+"F3.boolean.opBoolean","COPY",FACE,{"derivedFrom":makeQuery(id+"F3.opExtrude","CAP_FACE",FACE,{"disambiguationData":[OSD([sQuery(id+"F2.wireOp",EDGE,"E3.2.0.4"),sQuery(id+"F2.wireOp",EDGE,"E3.2.0.5"),sQuery(id+"F2.wireOp",EDGE,"E3.2.0.6"),sQuery(id+"F2.wireOp",EDGE,"E3.2.0.8")])],"isStart":false})});
            var Q19;
            Q19=makeQuery(id+"F3.boolean.opBoolean","COPY",FACE,{"derivedFrom":makeQuery(id+"F3.opExtrude","CAP_FACE",FACE,{"disambiguationData":[OSD([sQuery(id+"F2.wireOp",EDGE,"E1.bottom"),sQuery(id+"F2.wireOp",EDGE,"E1.top"),sQuery(id+"F2.wireOp",EDGE,"E1.left"),sQuery(id+"F2.wireOp",EDGE,"E1.right")])],"isStart":false})});
            var Q20;
            Q20=makeQuery(id+"F3.boolean.opBoolean","COPY",EDGE,{"derivedFrom":makeQuery(id+"F3.opExtrude","CAP_EDGE",EDGE,{"disambiguationData":[OSD([sQuery(id+"F2.wireOp",EDGE,"E3.2.0.12")])],"isStart":false})});
            var Q21;
            Q21=makeQuery(id+"F3.boolean.opBoolean","COPY",FACE,{"derivedFrom":makeQuery(id+"F3.opExtrude","CAP_FACE",FACE,{"disambiguationData":[OSD([sQuery(id+"F2.wireOp",EDGE,"2d819ab5-a139-4a24-9444-a94bec9d9159.0.2.2"),sQuery(id+"F2.wireOp",EDGE,"2d819ab5-a139-4a24-9444-a94bec9d9159.0.2.3"),sQuery(id+"F2.wireOp",EDGE,"2d819ab5-a139-4a24-9444-a94bec9d9159.0.2.4"),sQuery(id+"F2.wireOp",EDGE,"2d819ab5-a139-4a24-9444-a94bec9d9159.0.2.5")])],"isStart":false})});
            var Q22;
            Q22=makeQuery(id+"F3.boolean.opBoolean","COPY",FACE,{"derivedFrom":makeQuery(id+"F3.opExtrude","CAP_FACE",FACE,{"disambiguationData":[OSD([sQuery(id+"F2.wireOp",EDGE,"E3.2.0.12"),sQuery(id+"F2.wireOp",EDGE,"E3.2.0.14"),sQuery(id+"F2.wireOp",EDGE,"E3.2.0.17"),sQuery(id+"F2.wireOp",EDGE,"E3.2.0.20")])],"isStart":false})});
            var Q23;
            Q23=makeQuery(id+"F3.boolean.opBoolean","COPY",FACE,{"derivedFrom":makeQuery(id+"F3.opExtrude","CAP_FACE",FACE,{"disambiguationData":[OSD([sQuery(id+"F2.wireOp",EDGE,"2d819ab5-a139-4a24-9444-a94bec9d9159.0.2.0"),sQuery(id+"F2.wireOp",EDGE,"2d819ab5-a139-4a24-9444-a94bec9d9159.0.2.1"),sQuery(id+"F2.wireOp",EDGE,"2d819ab5-a139-4a24-9444-a94bec9d9159.0.2.6"),sQuery(id+"F2.wireOp",EDGE,"2d819ab5-a139-4a24-9444-a94bec9d9159.0.2.7")])],"isStart":false})});
            var Q24;
            Q24=makeQuery(id+"F3.boolean.opBoolean","COPY",FACE,{"derivedFrom":makeQuery(id+"F3.opExtrude","CAP_FACE",FACE,{"disambiguationData":[OSD([sQuery(id+"F2.wireOp",EDGE,"2d819ab5-a139-4a24-9444-a94bec9d9159.0.1.0"),sQuery(id+"F2.wireOp",EDGE,"2d819ab5-a139-4a24-9444-a94bec9d9159.0.1.1"),sQuery(id+"F2.wireOp",EDGE,"2d819ab5-a139-4a24-9444-a94bec9d9159.0.1.6"),sQuery(id+"F2.wireOp",EDGE,"2d819ab5-a139-4a24-9444-a94bec9d9159.0.1.7")])],"isStart":false})});
            var Q25;
            Q25=makeQuery(id+"F3.boolean.opBoolean","COPY",FACE,{"derivedFrom":makeQuery(id+"F3.opExtrude","CAP_FACE",FACE,{"disambiguationData":[OSD([sQuery(id+"F2.wireOp",EDGE,"2d819ab5-a139-4a24-9444-a94bec9d9159.0.1.2"),sQuery(id+"F2.wireOp",EDGE,"2d819ab5-a139-4a24-9444-a94bec9d9159.0.1.3"),sQuery(id+"F2.wireOp",EDGE,"2d819ab5-a139-4a24-9444-a94bec9d9159.0.1.4"),sQuery(id+"F2.wireOp",EDGE,"2d819ab5-a139-4a24-9444-a94bec9d9159.0.1.5")])],"isStart":false})});
            var Q26;
            Q26=makeQuery(id+"F3.boolean.opBoolean","COPY",FACE,{"derivedFrom":makeQuery(id+"F3.opExtrude","CAP_FACE",FACE,{"disambiguationData":[OSD([sQuery(id+"F2.wireOp",EDGE,"E3.1.0.12"),sQuery(id+"F2.wireOp",EDGE,"E3.1.0.14"),sQuery(id+"F2.wireOp",EDGE,"E3.1.0.17"),sQuery(id+"F2.wireOp",EDGE,"E3.1.0.20")])],"isStart":false})});
            var Q27;
            Q27=makeQuery(id+"F3.boolean.opBoolean","COPY",FACE,{"derivedFrom":makeQuery(id+"F3.opExtrude","CAP_FACE",FACE,{"disambiguationData":[OSD([sQuery(id+"F2.wireOp",EDGE,"E2.5.0.0"),sQuery(id+"F2.wireOp",EDGE,"E2.5.0.1"),sQuery(id+"F2.wireOp",EDGE,"E2.5.0.2"),sQuery(id+"F2.wireOp",EDGE,"E2.5.0.3")])],"isStart":false})});
            var Q28;
            Q28=makeQuery(id+"F3.boolean.opBoolean","COPY",FACE,{"derivedFrom":makeQuery(id+"F3.opExtrude","CAP_FACE",FACE,{"disambiguationData":[OSD([sQuery(id+"F2.wireOp",EDGE,"c4168fa5-6cb4-4a63-8e2b-b4d674aba8b3.0.7.0"),sQuery(id+"F2.wireOp",EDGE,"c4168fa5-6cb4-4a63-8e2b-b4d674aba8b3.3.7.0"),sQuery(id+"F2.wireOp",EDGE,"c4168fa5-6cb4-4a63-8e2b-b4d674aba8b3.6.7.0"),sQuery(id+"F2.wireOp",EDGE,"c4168fa5-6cb4-4a63-8e2b-b4d674aba8b3.9.7.0")])],"isStart":false})});
            var Q29;
            Q29=makeQuery(id+"F3.boolean.opBoolean","COPY",FACE,{"derivedFrom":makeQuery(id+"F3.opExtrude","CAP_FACE",FACE,{"disambiguationData":[OSD([sQuery(id+"F2.wireOp",EDGE,"c4168fa5-6cb4-4a63-8e2b-b4d674aba8b3.0.6.0"),sQuery(id+"F2.wireOp",EDGE,"c4168fa5-6cb4-4a63-8e2b-b4d674aba8b3.3.6.0"),sQuery(id+"F2.wireOp",EDGE,"c4168fa5-6cb4-4a63-8e2b-b4d674aba8b3.6.6.0"),sQuery(id+"F2.wireOp",EDGE,"c4168fa5-6cb4-4a63-8e2b-b4d674aba8b3.9.6.0")])],"isStart":false})});
            var Q30;
            Q30=makeQuery(id+"F3.boolean.opBoolean","COPY",FACE,{"derivedFrom":makeQuery(id+"F3.opExtrude","CAP_FACE",FACE,{"disambiguationData":[OSD([sQuery(id+"F2.wireOp",EDGE,"E4.12.3.0"),sQuery(id+"F2.wireOp",EDGE,"E4.15.3.0"),sQuery(id+"F2.wireOp",EDGE,"E4.18.3.0"),sQuery(id+"F2.wireOp",EDGE,"E4.24.3.0")])],"isStart":false})});
            var Q31;
            Q31=makeQuery(id+"F3.boolean.opBoolean","COPY",FACE,{"derivedFrom":makeQuery(id+"F3.opExtrude","CAP_FACE",FACE,{"disambiguationData":[OSD([sQuery(id+"F2.wireOp",EDGE,"E4.45.3.0"),sQuery(id+"F2.wireOp",EDGE,"E4.48.3.0"),sQuery(id+"F2.wireOp",EDGE,"E4.63.3.0"),sQuery(id+"F2.wireOp",EDGE,"E4.72.3.0")])],"isStart":false})});
            var Q32;
            Q32=makeQuery(id+"F3.boolean.opBoolean","COPY",FACE,{"derivedFrom":makeQuery(id+"F3.opExtrude","CAP_FACE",FACE,{"disambiguationData":[OSD([sQuery(id+"F2.wireOp",EDGE,"E4.0.3.0"),sQuery(id+"F2.wireOp",EDGE,"E4.3.3.0"),sQuery(id+"F2.wireOp",EDGE,"E4.6.3.0"),sQuery(id+"F2.wireOp",EDGE,"E4.9.3.0")])],"isStart":false})});
            var Q33;
            Q33=makeQuery(id+"F3.boolean.opBoolean","COPY",FACE,{"derivedFrom":makeQuery(id+"F3.opExtrude","CAP_FACE",FACE,{"disambiguationData":[OSD([sQuery(id+"F2.wireOp",EDGE,"E4.21.3.0"),sQuery(id+"F2.wireOp",EDGE,"E4.27.3.0"),sQuery(id+"F2.wireOp",EDGE,"E4.54.3.0"),sQuery(id+"F2.wireOp",EDGE,"E4.57.3.0")])],"isStart":false})});
            var Q34;
            Q34=makeQuery(id+"F3.boolean.opBoolean","COPY",FACE,{"derivedFrom":makeQuery(id+"F3.opExtrude","CAP_FACE",FACE,{"disambiguationData":[OSD([sQuery(id+"F2.wireOp",EDGE,"E4.30.3.0"),sQuery(id+"F2.wireOp",EDGE,"E4.33.3.0"),sQuery(id+"F2.wireOp",EDGE,"E4.39.3.0"),sQuery(id+"F2.wireOp",EDGE,"E4.66.3.0")])],"isStart":false})});
            var Q35;
            Q35=makeQuery(id+"F3.boolean.opBoolean","COPY",FACE,{"derivedFrom":makeQuery(id+"F3.opExtrude","CAP_FACE",FACE,{"disambiguationData":[OSD([sQuery(id+"F2.wireOp",EDGE,"E4.36.3.0"),sQuery(id+"F2.wireOp",EDGE,"E4.42.3.0"),sQuery(id+"F2.wireOp",EDGE,"E4.51.3.0"),sQuery(id+"F2.wireOp",EDGE,"E4.60.3.0")])],"isStart":false})});
            fillet(context, id + "F5", {"entities" : qUnion([Q0, Q1, Q2, Q3, Q4, Q5, Q6, Q7, Q8, Q9, Q10, Q11, Q12, Q13, Q14, Q15, Q16, Q17, Q18, Q19, Q20, Q21, Q22, Q23, Q24, Q25, Q26, Q27, Q28, Q29, Q30, Q31, Q32, Q33, Q34, Q35]), "radius" : 1 * mm, "tangentPropagation" : true, "allowEdgeOverflow" : false});
        }
        {
            var Q0;
            Q0=makeQuery(id+"F3.boolean.opBoolean","COPY",FACE,{"derivedFrom":makeQuery(id+"F3.opExtrude","SWEPT_FACE",FACE,{"disambiguationData":[OSD([sQuery(id+"F2.wireOp",EDGE,"E3.2.0.4")])]})});
            var Q1;
            Q1=makeQuery(id+"F3.boolean.opBoolean","COPY",FACE,{"derivedFrom":makeQuery(id+"F3.opExtrude","SWEPT_FACE",FACE,{"disambiguationData":[OSD([sQuery(id+"F2.wireOp",EDGE,"E3.2.0.5")])]})});
            var Q2;
            Q2=makeQuery(id+"F3.boolean.opBoolean","COPY",FACE,{"derivedFrom":makeQuery(id+"F3.opExtrude","SWEPT_FACE",FACE,{"disambiguationData":[OSD([sQuery(id+"F2.wireOp",EDGE,"E3.1.0.5")])]})});
            var Q3;
            Q3=makeQuery(id+"F3.boolean.opBoolean","COPY",FACE,{"derivedFrom":makeQuery(id+"F3.opExtrude","SWEPT_FACE",FACE,{"disambiguationData":[OSD([sQuery(id+"F2.wireOp",EDGE,"E1.left")])]})});
            var Q4;
            Q4=makeQuery(id+"F3.boolean.opBoolean","COPY",FACE,{"derivedFrom":makeQuery(id+"F3.opExtrude","SWEPT_FACE",FACE,{"disambiguationData":[OSD([sQuery(id+"F2.wireOp",EDGE,"E3.1.0.4")])]})});
            var Q5;
            Q5=makeQuery(id+"F3.boolean.opBoolean","COPY",FACE,{"derivedFrom":makeQuery(id+"F3.opExtrude","SWEPT_FACE",FACE,{"disambiguationData":[OSD([sQuery(id+"F2.wireOp",EDGE,"E1.right")])]})});
            var Q6;
            Q6=makeQuery(id+"F3.boolean.opBoolean","COPY",FACE,{"derivedFrom":makeQuery(id+"F3.opExtrude","SWEPT_FACE",FACE,{"disambiguationData":[OSD([sQuery(id+"F2.wireOp",EDGE,"E2.1.0.0")])]})});
            var Q7;
            Q7=makeQuery(id+"F3.boolean.opBoolean","COPY",FACE,{"derivedFrom":makeQuery(id+"F3.opExtrude","SWEPT_FACE",FACE,{"disambiguationData":[OSD([sQuery(id+"F2.wireOp",EDGE,"E3.1.0.15")])]})});
            var Q8;
            Q8=makeQuery(id+"F3.boolean.opBoolean","COPY",FACE,{"derivedFrom":makeQuery(id+"F3.opExtrude","SWEPT_FACE",FACE,{"disambiguationData":[OSD([sQuery(id+"F2.wireOp",EDGE,"E3.2.0.15")])]})});
            var Q9;
            Q9=makeQuery(id+"F3.boolean.opBoolean","COPY",FACE,{"derivedFrom":makeQuery(id+"F3.opExtrude","SWEPT_FACE",FACE,{"disambiguationData":[OSD([sQuery(id+"F2.wireOp",EDGE,"E3.2.0.21")])]})});
            var Q10;
            Q10=makeQuery(id+"F3.boolean.opBoolean","COPY",FACE,{"derivedFrom":makeQuery(id+"F3.opExtrude","SWEPT_FACE",FACE,{"disambiguationData":[OSD([sQuery(id+"F2.wireOp",EDGE,"E3.1.0.21")])]})});
            var Q11;
            Q11=makeQuery(id+"F3.boolean.opBoolean","COPY",FACE,{"derivedFrom":makeQuery(id+"F3.opExtrude","SWEPT_FACE",FACE,{"disambiguationData":[OSD([sQuery(id+"F2.wireOp",EDGE,"E2.1.0.2")])]})});
            var Q12;
            Q12=makeQuery(id+"F3.boolean.opBoolean","COPY",FACE,{"derivedFrom":makeQuery(id+"F3.opExtrude","SWEPT_FACE",FACE,{"disambiguationData":[OSD([sQuery(id+"F2.wireOp",EDGE,"E2.2.0.2")])]})});
            var Q13;
            Q13=makeQuery(id+"F3.boolean.opBoolean","COPY",FACE,{"derivedFrom":makeQuery(id+"F3.opExtrude","SWEPT_FACE",FACE,{"disambiguationData":[OSD([sQuery(id+"F2.wireOp",EDGE,"E3.1.0.1")])]})});
            var Q14;
            Q14=makeQuery(id+"F3.boolean.opBoolean","COPY",FACE,{"derivedFrom":makeQuery(id+"F3.opExtrude","SWEPT_FACE",FACE,{"disambiguationData":[OSD([sQuery(id+"F2.wireOp",EDGE,"E3.2.0.1")])]})});
            var Q15;
            Q15=makeQuery(id+"F3.boolean.opBoolean","COPY",FACE,{"derivedFrom":makeQuery(id+"F3.opExtrude","SWEPT_FACE",FACE,{"disambiguationData":[OSD([sQuery(id+"F2.wireOp",EDGE,"E3.1.0.7")])]})});
            var Q16;
            Q16=makeQuery(id+"F3.boolean.opBoolean","COPY",FACE,{"derivedFrom":makeQuery(id+"F3.opExtrude","SWEPT_FACE",FACE,{"disambiguationData":[OSD([sQuery(id+"F2.wireOp",EDGE,"E2.3.0.2")])]})});
            var Q17;
            Q17=makeQuery(id+"F3.boolean.opBoolean","COPY",FACE,{"derivedFrom":makeQuery(id+"F3.opExtrude","SWEPT_FACE",FACE,{"disambiguationData":[OSD([sQuery(id+"F2.wireOp",EDGE,"E3.2.0.7")])]})});
            var Q18;
            Q18=makeQuery(id+"F3.boolean.opBoolean","COPY",FACE,{"derivedFrom":makeQuery(id+"F3.opExtrude","SWEPT_FACE",FACE,{"disambiguationData":[OSD([sQuery(id+"F2.wireOp",EDGE,"E3.1.0.3")])]})});
            var Q19;
            Q19=makeQuery(id+"F3.boolean.opBoolean","COPY",FACE,{"derivedFrom":makeQuery(id+"F3.opExtrude","SWEPT_FACE",FACE,{"disambiguationData":[OSD([sQuery(id+"F2.wireOp",EDGE,"E3.2.0.3")])]})});
            var Q20;
            Q20=makeQuery(id+"F3.boolean.opBoolean","COPY",FACE,{"derivedFrom":makeQuery(id+"F3.opExtrude","SWEPT_FACE",FACE,{"disambiguationData":[OSD([sQuery(id+"F2.wireOp",EDGE,"E3.2.0.19")])]})});
            var Q21;
            Q21=makeQuery(id+"F3.boolean.opBoolean","COPY",FACE,{"derivedFrom":makeQuery(id+"F3.opExtrude","SWEPT_FACE",FACE,{"disambiguationData":[OSD([sQuery(id+"F2.wireOp",EDGE,"E3.1.0.19")])]})});
            var Q22;
            Q22=makeQuery(id+"F3.boolean.opBoolean","COPY",FACE,{"derivedFrom":makeQuery(id+"F3.opExtrude","SWEPT_FACE",FACE,{"disambiguationData":[OSD([sQuery(id+"F2.wireOp",EDGE,"E2.2.0.0")])]})});
            var Q23;
            Q23=makeQuery(id+"F3.boolean.opBoolean","COPY",FACE,{"derivedFrom":makeQuery(id+"F3.opExtrude","SWEPT_FACE",FACE,{"disambiguationData":[OSD([sQuery(id+"F2.wireOp",EDGE,"E2.3.0.0")])]})});
            var Q24;
            Q24=makeQuery(id+"F3.boolean.opBoolean","COPY",FACE,{"derivedFrom":makeQuery(id+"F3.opExtrude","SWEPT_FACE",FACE,{"disambiguationData":[OSD([sQuery(id+"F2.wireOp",EDGE,"E2.4.0.0")])]})});
            var Q25;
            Q25=makeQuery(id+"F3.boolean.opBoolean","COPY",FACE,{"derivedFrom":makeQuery(id+"F3.opExtrude","SWEPT_FACE",FACE,{"disambiguationData":[OSD([sQuery(id+"F2.wireOp",EDGE,"E3.1.0.11")])]})});
            var Q26;
            Q26=makeQuery(id+"F3.boolean.opBoolean","COPY",FACE,{"derivedFrom":makeQuery(id+"F3.opExtrude","SWEPT_FACE",FACE,{"disambiguationData":[OSD([sQuery(id+"F2.wireOp",EDGE,"E3.2.0.11")])]})});
            var Q27;
            Q27=makeQuery(id+"F3.boolean.opBoolean","COPY",FACE,{"derivedFrom":makeQuery(id+"F3.opExtrude","SWEPT_FACE",FACE,{"disambiguationData":[OSD([sQuery(id+"F2.wireOp",EDGE,"E3.1.0.10")])]})});
            var Q28;
            Q28=makeQuery(id+"F3.boolean.opBoolean","COPY",FACE,{"derivedFrom":makeQuery(id+"F3.opExtrude","SWEPT_FACE",FACE,{"disambiguationData":[OSD([sQuery(id+"F2.wireOp",EDGE,"E3.2.0.10")])]})});
            var Q29;
            Q29=makeQuery(id+"F3.boolean.opBoolean","COPY",FACE,{"derivedFrom":makeQuery(id+"F3.opExtrude","SWEPT_FACE",FACE,{"disambiguationData":[OSD([sQuery(id+"F2.wireOp",EDGE,"E2.4.0.2")])]})});
            var Q30;
            Q30=makeQuery(id+"F3.boolean.opBoolean","COPY",FACE,{"derivedFrom":makeQuery(id+"F3.opExtrude","SWEPT_FACE",FACE,{"disambiguationData":[OSD([sQuery(id+"F2.wireOp",EDGE,"E2.5.0.1")])]})});
            var Q31;
            Q31=makeQuery(id+"F3.boolean.opBoolean","COPY",FACE,{"derivedFrom":makeQuery(id+"F3.opExtrude","SWEPT_FACE",FACE,{"disambiguationData":[OSD([sQuery(id+"F2.wireOp",EDGE,"E3.1.0.12")])]})});
            var Q32;
            Q32=makeQuery(id+"F3.boolean.opBoolean","COPY",FACE,{"derivedFrom":makeQuery(id+"F3.opExtrude","SWEPT_FACE",FACE,{"disambiguationData":[OSD([sQuery(id+"F2.wireOp",EDGE,"E3.2.0.12")])]})});
            var Q33;
            Q33=makeQuery(id+"F3.boolean.opBoolean","COPY",FACE,{"derivedFrom":makeQuery(id+"F3.opExtrude","SWEPT_FACE",FACE,{"disambiguationData":[OSD([sQuery(id+"F2.wireOp",EDGE,"2d819ab5-a139-4a24-9444-a94bec9d9159.0.2.3")])]})});
            var Q34;
            Q34=makeQuery(id+"F3.boolean.opBoolean","COPY",FACE,{"derivedFrom":makeQuery(id+"F3.opExtrude","SWEPT_FACE",FACE,{"disambiguationData":[OSD([sQuery(id+"F2.wireOp",EDGE,"2d819ab5-a139-4a24-9444-a94bec9d9159.0.2.6")])]})});
            var Q35;
            Q35=makeQuery(id+"F3.boolean.opBoolean","COPY",FACE,{"derivedFrom":makeQuery(id+"F3.opExtrude","SWEPT_FACE",FACE,{"disambiguationData":[OSD([sQuery(id+"F2.wireOp",EDGE,"2d819ab5-a139-4a24-9444-a94bec9d9159.0.1.6")])]})});
            var Q36;
            Q36=makeQuery(id+"F3.boolean.opBoolean","COPY",FACE,{"derivedFrom":makeQuery(id+"F3.opExtrude","SWEPT_FACE",FACE,{"disambiguationData":[OSD([sQuery(id+"F2.wireOp",EDGE,"2d819ab5-a139-4a24-9444-a94bec9d9159.0.1.3")])]})});
            var Q37;
            Q37=makeQuery(id+"F3.boolean.opBoolean","COPY",FACE,{"derivedFrom":makeQuery(id+"F3.opExtrude","SWEPT_FACE",FACE,{"disambiguationData":[OSD([sQuery(id+"F2.wireOp",EDGE,"c4168fa5-6cb4-4a63-8e2b-b4d674aba8b3.3.6.0")])]})});
            var Q38;
            Q38=makeQuery(id+"F3.boolean.opBoolean","COPY",FACE,{"derivedFrom":makeQuery(id+"F3.opExtrude","SWEPT_FACE",FACE,{"disambiguationData":[OSD([sQuery(id+"F2.wireOp",EDGE,"E2.5.0.3")])]})});
            var Q39;
            Q39=makeQuery(id+"F3.boolean.opBoolean","COPY",FACE,{"derivedFrom":makeQuery(id+"F3.opExtrude","SWEPT_FACE",FACE,{"disambiguationData":[OSD([sQuery(id+"F2.wireOp",EDGE,"c4168fa5-6cb4-4a63-8e2b-b4d674aba8b3.9.6.0")])]})});
            var Q40;
            Q40=makeQuery(id+"F3.boolean.opBoolean","COPY",FACE,{"derivedFrom":makeQuery(id+"F3.opExtrude","SWEPT_FACE",FACE,{"disambiguationData":[OSD([sQuery(id+"F2.wireOp",EDGE,"c4168fa5-6cb4-4a63-8e2b-b4d674aba8b3.9.7.0")])]})});
            var Q41;
            Q41=makeQuery(id+"F3.boolean.opBoolean","COPY",FACE,{"derivedFrom":makeQuery(id+"F3.opExtrude","SWEPT_FACE",FACE,{"disambiguationData":[OSD([sQuery(id+"F2.wireOp",EDGE,"2d819ab5-a139-4a24-9444-a94bec9d9159.0.1.0")])]})});
            var Q42;
            Q42=makeQuery(id+"F3.boolean.opBoolean","COPY",FACE,{"derivedFrom":makeQuery(id+"F3.opExtrude","SWEPT_FACE",FACE,{"disambiguationData":[OSD([sQuery(id+"F2.wireOp",EDGE,"2d819ab5-a139-4a24-9444-a94bec9d9159.0.1.4")])]})});
            var Q43;
            Q43=makeQuery(id+"F3.boolean.opBoolean","COPY",FACE,{"derivedFrom":makeQuery(id+"F3.opExtrude","SWEPT_FACE",FACE,{"disambiguationData":[OSD([sQuery(id+"F2.wireOp",EDGE,"E3.1.0.17")])]})});
            var Q44;
            Q44=makeQuery(id+"F3.boolean.opBoolean","COPY",FACE,{"derivedFrom":makeQuery(id+"F3.opExtrude","SWEPT_FACE",FACE,{"disambiguationData":[OSD([sQuery(id+"F2.wireOp",EDGE,"E3.2.0.17")])]})});
            var Q45;
            Q45=makeQuery(id+"F3.boolean.opBoolean","COPY",FACE,{"derivedFrom":makeQuery(id+"F3.opExtrude","SWEPT_FACE",FACE,{"disambiguationData":[OSD([sQuery(id+"F2.wireOp",EDGE,"2d819ab5-a139-4a24-9444-a94bec9d9159.0.2.4")])]})});
            var Q46;
            Q46=makeQuery(id+"F3.boolean.opBoolean","COPY",FACE,{"derivedFrom":makeQuery(id+"F3.opExtrude","SWEPT_FACE",FACE,{"disambiguationData":[OSD([sQuery(id+"F2.wireOp",EDGE,"2d819ab5-a139-4a24-9444-a94bec9d9159.0.2.0")])]})});
            var Q47;
            Q47=makeQuery(id+"F3.boolean.opBoolean","COPY",FACE,{"derivedFrom":makeQuery(id+"F3.opExtrude","SWEPT_FACE",FACE,{"disambiguationData":[OSD([sQuery(id+"F2.wireOp",EDGE,"E4.18.3.0")])]})});
            var Q48;
            Q48=makeQuery(id+"F3.boolean.opBoolean","COPY",FACE,{"derivedFrom":makeQuery(id+"F3.opExtrude","SWEPT_FACE",FACE,{"disambiguationData":[OSD([sQuery(id+"F2.wireOp",EDGE,"E4.48.3.0")])]})});
            var Q49;
            Q49=makeQuery(id+"F3.boolean.opBoolean","COPY",FACE,{"derivedFrom":makeQuery(id+"F3.opExtrude","SWEPT_FACE",FACE,{"disambiguationData":[OSD([sQuery(id+"F2.wireOp",EDGE,"E4.6.3.0")])]})});
            var Q50;
            Q50=makeQuery(id+"F3.boolean.opBoolean","COPY",FACE,{"derivedFrom":makeQuery(id+"F3.opExtrude","SWEPT_FACE",FACE,{"disambiguationData":[OSD([sQuery(id+"F2.wireOp",EDGE,"E4.27.3.0")])]})});
            var Q51;
            Q51=makeQuery(id+"F3.boolean.opBoolean","COPY",FACE,{"derivedFrom":makeQuery(id+"F3.opExtrude","SWEPT_FACE",FACE,{"disambiguationData":[OSD([sQuery(id+"F2.wireOp",EDGE,"E4.66.3.0")])]})});
            var Q52;
            Q52=makeQuery(id+"F3.boolean.opBoolean","COPY",FACE,{"derivedFrom":makeQuery(id+"F3.opExtrude","SWEPT_FACE",FACE,{"disambiguationData":[OSD([sQuery(id+"F2.wireOp",EDGE,"E4.36.3.0")])]})});
            var Q53;
            Q53=makeQuery(id+"F3.boolean.opBoolean","COPY",FACE,{"derivedFrom":makeQuery(id+"F3.opExtrude","SWEPT_FACE",FACE,{"disambiguationData":[OSD([sQuery(id+"F2.wireOp",EDGE,"E4.51.3.0")])]})});
            var Q54;
            Q54=makeQuery(id+"F3.boolean.opBoolean","COPY",FACE,{"derivedFrom":makeQuery(id+"F3.opExtrude","SWEPT_FACE",FACE,{"disambiguationData":[OSD([sQuery(id+"F2.wireOp",EDGE,"E4.39.3.0")])]})});
            var Q55;
            Q55=makeQuery(id+"F3.boolean.opBoolean","COPY",FACE,{"derivedFrom":makeQuery(id+"F3.opExtrude","SWEPT_FACE",FACE,{"disambiguationData":[OSD([sQuery(id+"F2.wireOp",EDGE,"E4.54.3.0")])]})});
            var Q56;
            Q56=makeQuery(id+"F3.boolean.opBoolean","COPY",FACE,{"derivedFrom":makeQuery(id+"F3.opExtrude","SWEPT_FACE",FACE,{"disambiguationData":[OSD([sQuery(id+"F2.wireOp",EDGE,"E4.0.3.0")])]})});
            var Q57;
            Q57=makeQuery(id+"F3.boolean.opBoolean","COPY",FACE,{"derivedFrom":makeQuery(id+"F3.opExtrude","SWEPT_FACE",FACE,{"disambiguationData":[OSD([sQuery(id+"F2.wireOp",EDGE,"E4.72.3.0")])]})});
            var Q58;
            Q58=makeQuery(id+"F3.boolean.opBoolean","COPY",FACE,{"derivedFrom":makeQuery(id+"F3.opExtrude","SWEPT_FACE",FACE,{"disambiguationData":[OSD([sQuery(id+"F2.wireOp",EDGE,"E4.24.3.0")])]})});
            fillet(context, id + "F6", {"entities" : qUnion([Q0, Q1, Q2, Q3, Q4, Q5, Q6, Q7, Q8, Q9, Q10, Q11, Q12, Q13, Q14, Q15, Q16, Q17, Q18, Q19, Q20, Q21, Q22, Q23, Q24, Q25, Q26, Q27, Q28, Q29, Q30, Q31, Q32, Q33, Q34, Q35, Q36, Q37, Q38, Q39, Q40, Q41, Q42, Q43, Q44, Q45, Q46, Q47, Q48, Q49, Q50, Q51, Q52, Q53, Q54, Q55, Q56, Q57, Q58]), "radius" : 0.5 * mm, "tangentPropagation" : true, "allowEdgeOverflow" : false});
        }
        {
            var Q0;
            Q0=makeQuery(id+"F1.opExtrude","CAP_FACE",FACE,{"disambiguationData":[OSD([sQuery(id+"F0.wireOp",EDGE,"E0.bottom"),sQuery(id+"F0.wireOp",EDGE,"E0.top"),sQuery(id+"F0.wireOp",EDGE,"E0.left"),sQuery(id+"F0.wireOp",EDGE,"E0.right")])],"isStart":true});
            shell(context, id + "F7", {"entities" : qUnion([Q0]), "thickness" : 1.5 * mm});
        }
    });
